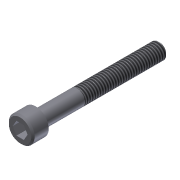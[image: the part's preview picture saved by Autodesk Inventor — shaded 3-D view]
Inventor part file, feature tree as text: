
AUTODESK INVENTOR PART (.ipt)
format: ipt  version: 2011 (Build 150239000, 239)  size: 102,912 bytes
history: native  units: in
note: dims shown in document units (in); Inventor stores cm internally (conversion verified against a paired STEP export)
features: extrude x3, sketch x3, chamfer x2, thread x1
ambient origin geometry x8: Origin, YZ Plane, XZ Plane, XY Plane, X Axis, Y Axis, Z Axis, Center Point
bodies: Solid1 (feature_tree)
feature tree (9):
  extrude  "Extrusion1"  Depth=0.19in TaperAngle=0.0deg
  extrude  "Extrusion2"  Depth=1.5in TaperAngle=0.0deg
  extrude  "Extrusion3"  Depth=0.125in TaperAngle=0.0deg
  thread  "Thread1"  [1 undecoded]
  chamfer  "Chamfer1"  Distance=0.02in Angle=45.0deg
  chamfer  "Chamfer2"  Distance=0.02in Angle=45.0deg
  sketch  "Sketch1"  dims[d0=0.312in d1=0.19in d2=0.0in]
  sketch  "Sketch2"  dims[d3=0.19in d4=1.5in d5=0.0in]
  sketch  "Sketch3"  dims[d6=0.1562in d7=0.125in d8=0.0in d9=1.0in d10=0.0in d11=0.02in d12=0.125in d13=45.0deg d14=0.02in d15=0.125in d16=45.0deg]
note: 1 required parameter value undecoded (feature->parameter linkage not recoverable at this tier; creation-order binding heuristic only, values carry confidence <= 0.55)
